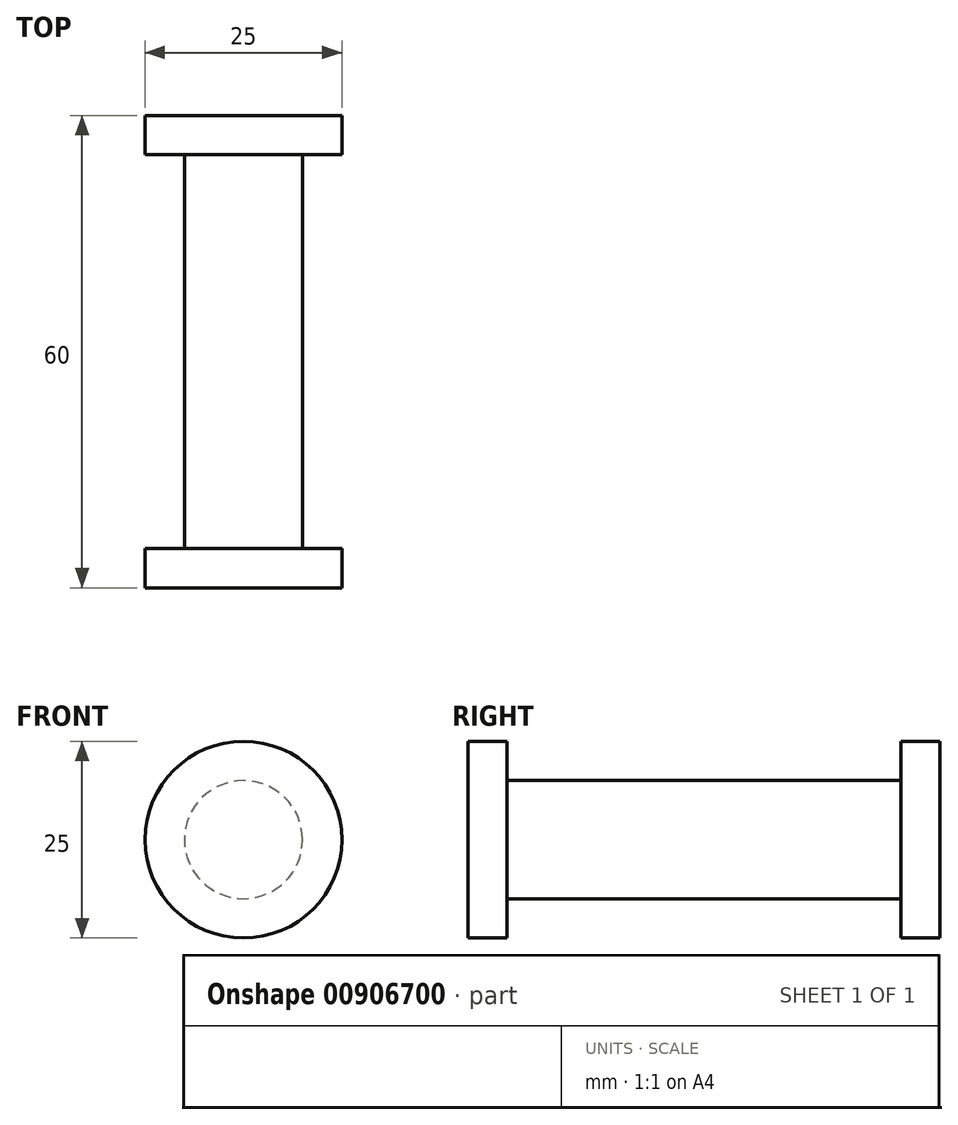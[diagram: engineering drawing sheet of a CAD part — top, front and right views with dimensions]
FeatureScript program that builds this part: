
annotation { "Feature Type Name" : "Feature", "Feature Type Description" : "" }
export const myFeature = defineFeature(function(context is Context, id is Id, definition is map)
    precondition{}
    {
        {
            var Q0;
            Q0=qCreatedBy(makeId("Front.planeOp"),FACE);
            var sketch = newSketch(context, id + "F0", { "sketchPlane" : qUnion([Q0])});
            skCircle(sketch, "E0", {"center": v(0, 0) * mm, "radius": 12.5 * mm});
            skCircle(sketch, "E1", {"center": v(0, 0) * mm, "radius": 7.5 * mm});
            skSolve(sketch);
        }
        {
            var Q0;
            Q0=makeQuery(id+"F0.imprint","IMPRINT",FACE,{"disambiguationData":[TD([[makeQuery(id+"F0.imprint","IMPRINT",EDGE,{"derivedFrom":sQuery(id+"F0.wireOp",EDGE,"E1")}),1.0]])]});
            extrude(context, id + "F1", {"entities" : qUnion([Q0]), "depth" : 60 * mm, "offsetDistance" : 25 * mm});
        }
        {
            var Q0;
            Q0=makeQuery(id+"F0.imprint","IMPRINT",FACE,{"disambiguationData":[TD([[makeQuery(id+"F0.imprint","IMPRINT",EDGE,{"derivedFrom":sQuery(id+"F0.wireOp",EDGE,"E0")}),1.0]])]});
            extrude(context, id + "F2", {"entities" : qUnion([Q0]), "operationType" : NewBodyOperationType.ADD, "depth" : 5 * mm, "offsetDistance" : 25 * mm});
        }
        {
            var Q0;
            Q0=makeQuery(id+"F0.imprint","IMPRINT",FACE,{"disambiguationData":[TD([[makeQuery(id+"F0.imprint","IMPRINT",EDGE,{"derivedFrom":sQuery(id+"F0.wireOp",EDGE,"E0")}),1.0]])]});
            extrude(context, id + "F3", {"entities" : qUnion([Q0]), "operationType" : NewBodyOperationType.ADD, "depth" : 60 * mm, "offsetDistance" : 25 * mm, "hasSecondDirection" : true, "secondDirectionOppositeDirection" : false, "secondDirectionDepth" : 55 * mm});
        }
    });
